# Revit family: g2021_EN_Fold-up-Door_Ferroflex_Windwall_D01478ES
name_source: partatom
category: Doors
units: mm (PartAtom-declared; Revit-internal decimal feet)

## family parameters
Always vertical = Yes
Cut with Voids When Loaded = No
Host = Wall
OmniClass Number = 23.30.10.00
OmniClass Title = Doors
Room Calculation Point = No
Shared = No

## types (1)
- Fold-up Door, 7000 x 7000 mm
    A = 200 mm  [stored 0.656168 ft]
    Analytic Construction = <Ninguno>
    Article Number = D01478ES-V0
    Assembly Place = On site
    Atmospheric Acidification Per Unit = 0
    B = 120 mm  [stored 0.393701 ft]
    BIM Content Download Platform = www.bimetica.com
    BIM Eelement Expiry Date = 2 years
    BIM Element Issue Date = 29/11/2022
    BIM Profile URL = https://bimetica.com
    BIM technical support = https://bimsupport.info
    C = 480 mm  [stored 1.5748 ft]
    CE Mark = Yes
    COBie Category = IfcDoor
    Clear Area to Access = 0 mm  [stored 0 ft]
    Clear Height = 7000 mm  [stored 22.9659 ft]
    Clear Width = 7000 mm  [stored 22.9659 ft]
    Climate Change Per Unit = 0
    Code = Windwall
    Container Material = Wooden box
    Control panel Height = 1200 mm  [stored 3.93701 ft]
    Curtain Material = PVC_Blue
    D = 100 mm  [stored 0.328084 ft]
    D1 = 400 mm  [stored 1.31234 ft]
    D2 = 800 mm  [stored 2.62467 ft]
    Declaration of Performance URL = https://ferroflexindustrialaccess.com
    Define Thermal Properties by = Schematic Type
    Description = Stacking type high-speed door with vertical opening, consisting of guides and head in lacquered steel, and PVC canvas, color to choose and with the possibility of transparent peepholes. Parameterizable control panel, active security by means of crossed photocells barrier.
    E = 100 mm  [stored 0.328084 ft]
    Energy Spent = 0
    Eutrophication Per Unit = 0
    Exterior Offset = 0 mm  [stored 0 ft]
    Finish = Estructura de hierro o Inox y lona de PVC
    Fire Rating = Lona ISO 3795-89
    FireExit = No
    Frame Projection Ext. = 25 mm  [stored 0.082021 ft]
    Frame Projection Int. = 25 mm  [stored 0.082021 ft]
    Function = Exterior
    G = 380 mm
    GDO-BIM Standard Version = GDO-BIM V02
    Glazing Area Fraction = 0
    Gubimclass Code = Puertas de acceso
    Gubimclass Title = 80.10.40.20
    HasDrive = Yes
    Hazardous Waste Per Unit = 0
    Height = 7000 mm  [stored 22.9659 ft]
    History = (RVT2021) Creation of Element.
    IfcExportAs = IfcDoor
    IfcExportType = Roll-up door
    Inert Waste Per Unit = 0
    Infiltration = 0
    Interior Offset = 0 mm  [stored 0 ft]
    Is Accesible = No
    Is Extended Warranty = No
    Is External = Yes
    License Number = XXX-XXXX7125
    Maintenance Cost = 0
    Manufacturer = Ferroflex S.L.U.
    Masterformat Code = 08 31 00
    Masterformat Title = Access Doors and Panels
    Material = Stainless Steel_Laquered
    Measuring Unit = Unit
    Minimum Required Height = 2100 mm  [stored 6.88976 ft]
    Model = Windwall
    Model Label = Windwall Fold-up Door
    No Panel = 16.3
    Non Renewable Energy Consumption Per Unit = 0
    NonHazardous Waste Per Unit = 0
    Omniclass Code = 23-17 11 27 13
    Omniclass Title = Access Doors
    Operation = Enrrollable
    Panel A = 8
    Panel B = 8
    Photochemical Ozone Formation Per Unit = 0
    Product URL = https://ferroflexindustrialaccess.com
    Radioactive Waste Per Unit = 0
    Reference = D01478ES-V0
    Renewable Energy Consumption Per Unit = 0
    Resource Depletion Per Unit = 0
    Safety Standard = 2006/42/CE
    Security Rating = ISO 1421 / ISO 13937-2
    Self Closing = No
    Series = Fold-up Door
    Sight glass area = Possibility of sight glass areas are available
    SmokeStop = No
    Stratospheric Ozone Layer Destruction Per Unit = 0
    Thickness = 100 mm  [stored 0.328084 ft]
    Total Primary Energy Consumption Per Unit = 0
    UNSPSC Code = 30171503
    UNSPSC Title = Rolling doors
    URL = https://ferroflexindustrialaccess.com
    Version = RVT2021
    Wall Closure = Interior
    Warranty Content = Materials
    Warranty Period = One year
    Water Consumption Per Unit = 0
    Weight = 0.00 kg
    Width = 7000 mm  [stored 22.9659 ft]
    Wind Load Rating = Clase 5 < 5x7mts < Clase 3
    Wrapping Material = Plastic wrapping

note: [stored X ft] marks values corroborated as IEEE doubles in the binary element streams (Revit-internal decimal feet)

## geometry (parser evidence)
native form markers: Sweep x5
no freeform markers — native parametric forms only
